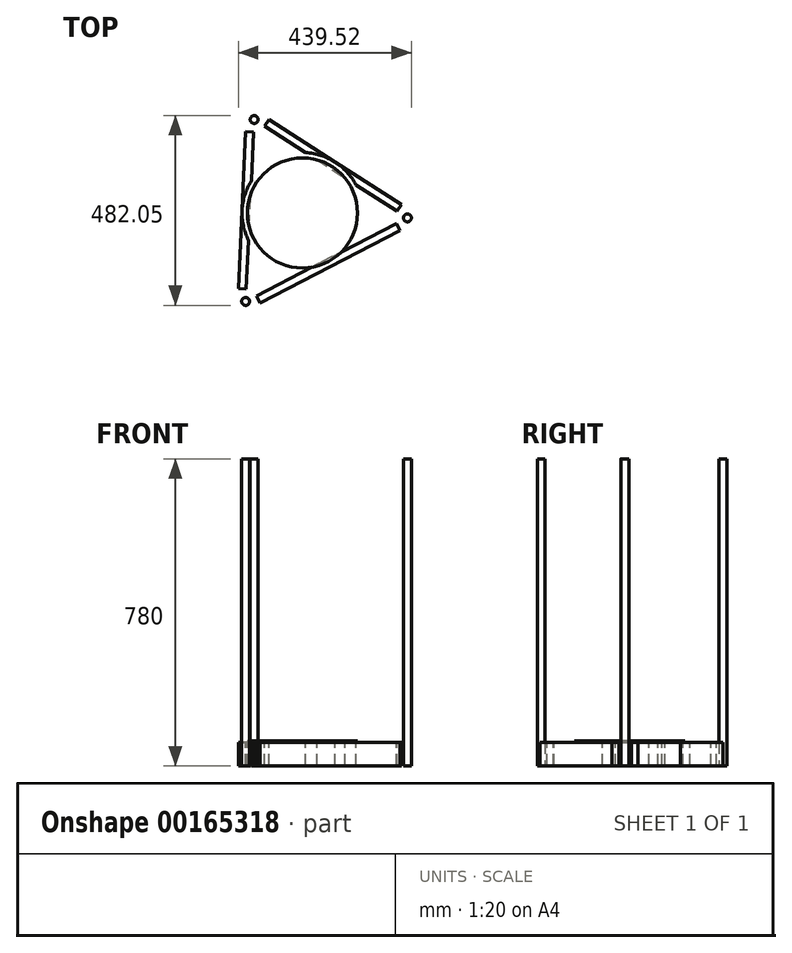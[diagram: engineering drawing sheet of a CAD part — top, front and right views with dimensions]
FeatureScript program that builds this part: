
annotation { "Feature Type Name" : "Feature", "Feature Type Description" : "" }
export const myFeature = defineFeature(function(context is Context, id is Id, definition is map)
    precondition{}
    {
        {
            var Q0;
            Q0=qCreatedBy(makeId("Top.planeOp"),FACE);
            var sketch = newSketch(context, id + "F0", { "sketchPlane" : qUnion([Q0])});
            skCircle(sketch, "E0", {"center": v(0, 0) * mm, "radius": 133.53 * mm});
            skCircle(sketch, "E1.cCircle", {"center": v(0, 0) * mm, "radius": 133.53 * mm, "construction": true});
            skLineSegment(sketch, "E1.0", {"start": v(-122.5, 237.3) * mm, "end": v(266.76, -12.56) * mm});
            skLineSegment(sketch, "E1.1", {"start": v(266.76, -12.56) * mm, "end": v(-144.26, -224.75) * mm});
            skLineSegment(sketch, "E1.2", {"start": v(-144.26, -224.75) * mm, "end": v(-122.5, 237.3) * mm});
            skPoint(sketch, "E1.0.midPoint", {"position": v(72.13, 112.37) * mm});
            skPoint(sketch, "E2", {"position": v(-116.46, -210.4) * mm});
            skPoint(sketch, "E3", {"position": v(238.97, -26.9) * mm});
            skLineSegment(sketch, "E4", {"start": v(238.97, -26.9) * mm, "end": v(248.14, -44.68) * mm});
            skLineSegment(sketch, "E5", {"start": v(248.14, -44.68) * mm, "end": v(-107.29, -228.17) * mm});
            skLineSegment(sketch, "E6", {"start": v(-107.29, -228.17) * mm, "end": v(-116.46, -210.4) * mm});
            skLineSegment(sketch, "E7.1.0", {"start": v(-85.38, 237.24) * mm, "end": v(251.24, 21.17) * mm});
            skLineSegment(sketch, "E7.1.1", {"start": v(-96.18, 220.4) * mm, "end": v(-85.38, 237.24) * mm});
            skLineSegment(sketch, "E7.1.2", {"start": v(251.24, 21.17) * mm, "end": v(240.44, 4.34) * mm});
            skPoint(sketch, "E7.1.3", {"position": v(-96.18, 220.4) * mm});
            skPoint(sketch, "E7.1.4", {"position": v(240.44, 4.34) * mm});
            skLineSegment(sketch, "E7.2.0", {"start": v(-162.76, -192.56) * mm, "end": v(-143.96, 207) * mm});
            skLineSegment(sketch, "E7.2.1", {"start": v(-142.79, -193.5) * mm, "end": v(-162.76, -192.56) * mm});
            skLineSegment(sketch, "E7.2.2", {"start": v(-143.96, 207) * mm, "end": v(-123.98, 206.06) * mm});
            skPoint(sketch, "E7.2.3", {"position": v(-142.79, -193.5) * mm});
            skPoint(sketch, "E7.2.4", {"position": v(-123.98, 206.06) * mm});
            skCircle(sketch, "E8", {"center": v(0, 0) * mm, "radius": 153.53 * mm});
            skCircle(sketch, "E9", {"center": v(266.76, -12.56) * mm, "radius": 10 * mm});
            skCircle(sketch, "E10.1.0", {"center": v(-122.5, 237.3) * mm, "radius": 10 * mm});
            skCircle(sketch, "E10.2.0", {"center": v(-144.26, -224.75) * mm, "radius": 10 * mm});
            skCircle(sketch, "E11", {"center": v(0, 0) * mm, "radius": 140 * mm});
            skSolve(sketch);
        }
        {
            var Q0;
            {var subQ0=sQuery(id+"F0.wireOp",EDGE,"E1.1");var subQ1=sQuery(id+"F0.wireOp",EDGE,"E1.0");var subQ2=makeQuery(id+"F0.imprint","INTERSECT",VERTEX,{"derivedFrom":[subQ1,subQ0]});Q0=makeQuery(id+"F0.imprint","IMPRINT",FACE,{"disambiguationData":[TD([[makeQuery(id+"F0.imprint","IMPRINT",EDGE,{"disambiguationData":[TD([[subQ2,1.0]])],"derivedFrom":subQ1}),1.0]])]});}
            var Q1;
            {var subQ0=sQuery(id+"F0.wireOp",EDGE,"E1.1");var subQ1=sQuery(id+"F0.wireOp",EDGE,"E1.0");var subQ2=makeQuery(id+"F0.imprint","INTERSECT",VERTEX,{"derivedFrom":[subQ1,subQ0]});Q1=makeQuery(id+"F0.imprint","IMPRINT",FACE,{"disambiguationData":[TD([[makeQuery(id+"F0.imprint","IMPRINT",EDGE,{"disambiguationData":[TD([[subQ2,1.0]])],"derivedFrom":subQ1}),-1.0]])]});}
            var Q2;
            {var subQ0=sQuery(id+"F0.wireOp",EDGE,"E1.2");var subQ1=sQuery(id+"F0.wireOp",EDGE,"E1.1");var subQ2=makeQuery(id+"F0.imprint","INTERSECT",VERTEX,{"derivedFrom":[subQ1,subQ0]});Q2=makeQuery(id+"F0.imprint","IMPRINT",FACE,{"disambiguationData":[TD([[makeQuery(id+"F0.imprint","IMPRINT",EDGE,{"disambiguationData":[TD([[subQ2,1.0]])],"derivedFrom":subQ1}),-1.0]])]});}
            var Q3;
            {var subQ0=sQuery(id+"F0.wireOp",EDGE,"E1.2");var subQ1=sQuery(id+"F0.wireOp",EDGE,"E1.1");var subQ2=makeQuery(id+"F0.imprint","INTERSECT",VERTEX,{"derivedFrom":[subQ1,subQ0]});Q3=makeQuery(id+"F0.imprint","IMPRINT",FACE,{"disambiguationData":[TD([[makeQuery(id+"F0.imprint","IMPRINT",EDGE,{"disambiguationData":[TD([[subQ2,1.0]])],"derivedFrom":subQ1}),1.0]])]});}
            var Q4;
            {var subQ0=sQuery(id+"F0.wireOp",EDGE,"E1.2");var subQ1=sQuery(id+"F0.wireOp",EDGE,"E1.0");var subQ2=makeQuery(id+"F0.imprint","INTERSECT",VERTEX,{"derivedFrom":[subQ1,subQ0]});Q4=makeQuery(id+"F0.imprint","IMPRINT",FACE,{"disambiguationData":[TD([[makeQuery(id+"F0.imprint","IMPRINT",EDGE,{"disambiguationData":[TD([[subQ2,-1.0]])],"derivedFrom":subQ1}),-1.0]])]});}
            var Q5;
            {var subQ0=sQuery(id+"F0.wireOp",EDGE,"E1.2");var subQ1=sQuery(id+"F0.wireOp",EDGE,"E1.0");var subQ2=makeQuery(id+"F0.imprint","INTERSECT",VERTEX,{"derivedFrom":[subQ1,subQ0]});Q5=makeQuery(id+"F0.imprint","IMPRINT",FACE,{"disambiguationData":[TD([[makeQuery(id+"F0.imprint","IMPRINT",EDGE,{"disambiguationData":[TD([[subQ2,-1.0]])],"derivedFrom":subQ1}),1.0]])]});}
            extrude(context, id + "F1", {"entities" : qUnion([Q0, Q1, Q2, Q3, Q4, Q5]), "offsetDistance" : 25 * mm, "depth" : 720 * mm, "hasSecondDirection" : true, "secondDirectionOppositeDirection" : true, "secondDirectionDepth" : 60 * mm});
        }
        {
            var Q0;
            {var subQ0=sQuery(id+"F0.wireOp",EDGE,"E6");Q0=makeQuery(id+"F0.imprint","IMPRINT",FACE,{"disambiguationData":[TD([[makeQuery(id+"F0.imprint","IMPRINT",EDGE,{"derivedFrom":subQ0}),-1.0]])]});}
            var Q1;
            {var subQ0=sQuery(id+"F0.wireOp",EDGE,"E7.2.2");Q1=makeQuery(id+"F0.imprint","IMPRINT",FACE,{"disambiguationData":[TD([[makeQuery(id+"F0.imprint","IMPRINT",EDGE,{"derivedFrom":subQ0}),-1.0]])]});}
            var Q2;
            {var subQ0=sQuery(id+"F0.wireOp",EDGE,"E7.1.1");Q2=makeQuery(id+"F0.imprint","IMPRINT",FACE,{"disambiguationData":[TD([[makeQuery(id+"F0.imprint","IMPRINT",EDGE,{"derivedFrom":subQ0}),-1.0]])]});}
            var Q3;
            {var subQ0=sQuery(id+"F0.wireOp",EDGE,"E7.1.2");Q3=makeQuery(id+"F0.imprint","IMPRINT",FACE,{"disambiguationData":[TD([[makeQuery(id+"F0.imprint","IMPRINT",EDGE,{"derivedFrom":subQ0}),-1.0]])]});}
            var Q4;
            {var subQ0=sQuery(id+"F0.wireOp",EDGE,"E1.0");var subQ1=makeQuery(id+"F0.imprint","INTERSECT",VERTEX,{"derivedFrom":[sQuery(id+"F0.wireOp",EDGE,"E0"),subQ0]});Q4=makeQuery(id+"F0.imprint","IMPRINT",FACE,{"disambiguationData":[TD([[makeQuery(id+"F0.imprint","IMPRINT",EDGE,{"disambiguationData":[TD([[subQ1,1.0]])],"derivedFrom":subQ0}),1.0]])]});}
            var Q5;
            {var subQ0=sQuery(id+"F0.wireOp",EDGE,"E1.2");var subQ1=makeQuery(id+"F0.imprint","INTERSECT",VERTEX,{"derivedFrom":[sQuery(id+"F0.wireOp",EDGE,"E0"),subQ0]});Q5=makeQuery(id+"F0.imprint","IMPRINT",FACE,{"disambiguationData":[TD([[makeQuery(id+"F0.imprint","IMPRINT",EDGE,{"disambiguationData":[TD([[subQ1,1.0]])],"derivedFrom":subQ0}),1.0]])]});}
            var Q6;
            {var subQ0=sQuery(id+"F0.wireOp",EDGE,"E7.2.1");Q6=makeQuery(id+"F0.imprint","IMPRINT",FACE,{"disambiguationData":[TD([[makeQuery(id+"F0.imprint","IMPRINT",EDGE,{"derivedFrom":subQ0}),-1.0]])]});}
            var Q7;
            {var subQ0=sQuery(id+"F0.wireOp",EDGE,"E4");Q7=makeQuery(id+"F0.imprint","IMPRINT",FACE,{"disambiguationData":[TD([[makeQuery(id+"F0.imprint","IMPRINT",EDGE,{"derivedFrom":subQ0}),-1.0]])]});}
            var Q8;
            {var subQ0=sQuery(id+"F0.wireOp",EDGE,"E1.1");var subQ1=makeQuery(id+"F0.imprint","INTERSECT",VERTEX,{"derivedFrom":[sQuery(id+"F0.wireOp",EDGE,"E0"),subQ0]});Q8=makeQuery(id+"F0.imprint","IMPRINT",FACE,{"disambiguationData":[TD([[makeQuery(id+"F0.imprint","IMPRINT",EDGE,{"disambiguationData":[TD([[subQ1,1.0]])],"derivedFrom":subQ0}),1.0]])]});}
            var Q9;
            {var subQ0=sQuery(id+"F0.wireOp",EDGE,"E8");var subQ2=sQuery(id+"F0.wireOp",EDGE,"E1.2");var subQ3=makeQuery(id+"F0.imprint","INTERSECT",VERTEX,{"disambiguationData":[OD(0.0)],"derivedFrom":[subQ2,subQ0]});Q9=makeQuery(id+"F0.imprint","IMPRINT",FACE,{"disambiguationData":[TD([[makeQuery(id+"F0.imprint","IMPRINT",EDGE,{"disambiguationData":[TD([[subQ3,-1.0]])],"derivedFrom":subQ2}),1.0]])]});}
            var Q10;
            {var subQ0=sQuery(id+"F0.wireOp",EDGE,"E8");var subQ2=sQuery(id+"F0.wireOp",EDGE,"E1.0");var subQ3=makeQuery(id+"F0.imprint","INTERSECT",VERTEX,{"disambiguationData":[OD(0.0)],"derivedFrom":[subQ2,subQ0]});Q10=makeQuery(id+"F0.imprint","IMPRINT",FACE,{"disambiguationData":[TD([[makeQuery(id+"F0.imprint","IMPRINT",EDGE,{"disambiguationData":[TD([[subQ3,-1.0]])],"derivedFrom":subQ2}),1.0]])]});}
            var Q11;
            {var subQ0=sQuery(id+"F0.wireOp",EDGE,"E8");var subQ2=sQuery(id+"F0.wireOp",EDGE,"E1.1");var subQ3=makeQuery(id+"F0.imprint","INTERSECT",VERTEX,{"disambiguationData":[OD(0.0)],"derivedFrom":[subQ2,subQ0]});Q11=makeQuery(id+"F0.imprint","IMPRINT",FACE,{"disambiguationData":[TD([[makeQuery(id+"F0.imprint","IMPRINT",EDGE,{"disambiguationData":[TD([[subQ3,-1.0]])],"derivedFrom":subQ2}),1.0]])]});}
            extrude(context, id + "F2", {"entities" : qUnion([Q0, Q1, Q2, Q3, Q4, Q5, Q6, Q7, Q8, Q9, Q10, Q11]), "oppositeDirection" : true, "depth" : 60 * mm});
        }
        {
            var Q0;
            {var subQ0=sQuery(id+"F0.wireOp",EDGE,"E1.2");var subQ1=sQuery(id+"F0.wireOp",EDGE,"E0");var subQ2=makeQuery(id+"F0.imprint","INTERSECT",VERTEX,{"derivedFrom":[subQ1,subQ0]});Q0=makeQuery(id+"F0.imprint","IMPRINT",FACE,{"disambiguationData":[TD([[makeQuery(id+"F0.imprint","IMPRINT",EDGE,{"disambiguationData":[TD([[subQ2,1.0]])],"derivedFrom":subQ1}),-1.0]])]});}
            var Q1;
            {var subQ0=sQuery(id+"F0.wireOp",EDGE,"E0");var subQ1=makeQuery(id+"F0.imprint","INTERSECT",VERTEX,{"derivedFrom":[subQ0,sQuery(id+"F0.wireOp",EDGE,"E1.2")]});Q1=makeQuery(id+"F0.imprint","IMPRINT",FACE,{"disambiguationData":[TD([[makeQuery(id+"F0.imprint","IMPRINT",EDGE,{"disambiguationData":[TD([[subQ1,1.0]])],"derivedFrom":subQ0}),1.0]])]});}
            var Q2;
            {var subQ0=sQuery(id+"F0.wireOp",EDGE,"E1.0");var subQ1=makeQuery(id+"F0.imprint","INTERSECT",VERTEX,{"derivedFrom":[sQuery(id+"F0.wireOp",EDGE,"E0"),subQ0]});Q2=makeQuery(id+"F0.imprint","IMPRINT",FACE,{"disambiguationData":[TD([[makeQuery(id+"F0.imprint","IMPRINT",EDGE,{"disambiguationData":[TD([[subQ1,1.0]])],"derivedFrom":subQ0}),1.0]])]});}
            var Q3;
            {var subQ0=sQuery(id+"F0.wireOp",EDGE,"E1.0");var subQ1=sQuery(id+"F0.wireOp",EDGE,"E0");var subQ2=makeQuery(id+"F0.imprint","INTERSECT",VERTEX,{"derivedFrom":[subQ1,subQ0]});Q3=makeQuery(id+"F0.imprint","IMPRINT",FACE,{"disambiguationData":[TD([[makeQuery(id+"F0.imprint","IMPRINT",EDGE,{"disambiguationData":[TD([[subQ2,1.0]])],"derivedFrom":subQ1}),-1.0]])]});}
            var Q4;
            {var subQ0=sQuery(id+"F0.wireOp",EDGE,"E1.2");var subQ1=sQuery(id+"F0.wireOp",EDGE,"E0");var subQ2=makeQuery(id+"F0.imprint","INTERSECT",VERTEX,{"derivedFrom":[subQ1,subQ0]});Q4=makeQuery(id+"F0.imprint","IMPRINT",FACE,{"disambiguationData":[TD([[makeQuery(id+"F0.imprint","IMPRINT",EDGE,{"disambiguationData":[TD([[subQ2,-1.0]])],"derivedFrom":subQ1}),-1.0]])]});}
            var Q5;
            {var subQ0=sQuery(id+"F0.wireOp",EDGE,"E1.2");var subQ1=makeQuery(id+"F0.imprint","INTERSECT",VERTEX,{"derivedFrom":[sQuery(id+"F0.wireOp",EDGE,"E0"),subQ0]});Q5=makeQuery(id+"F0.imprint","IMPRINT",FACE,{"disambiguationData":[TD([[makeQuery(id+"F0.imprint","IMPRINT",EDGE,{"disambiguationData":[TD([[subQ1,1.0]])],"derivedFrom":subQ0}),1.0]])]});}
            var Q6;
            {var subQ0=sQuery(id+"F0.wireOp",EDGE,"E1.1");var subQ1=makeQuery(id+"F0.imprint","INTERSECT",VERTEX,{"derivedFrom":[sQuery(id+"F0.wireOp",EDGE,"E0"),subQ0]});Q6=makeQuery(id+"F0.imprint","IMPRINT",FACE,{"disambiguationData":[TD([[makeQuery(id+"F0.imprint","IMPRINT",EDGE,{"disambiguationData":[TD([[subQ1,1.0]])],"derivedFrom":subQ0}),1.0]])]});}
            extrude(context, id + "F3", {"entities" : qUnion([Q0, Q1, Q2, Q3, Q4, Q5, Q6]), "depth" : 4 * mm});
        }
    });
